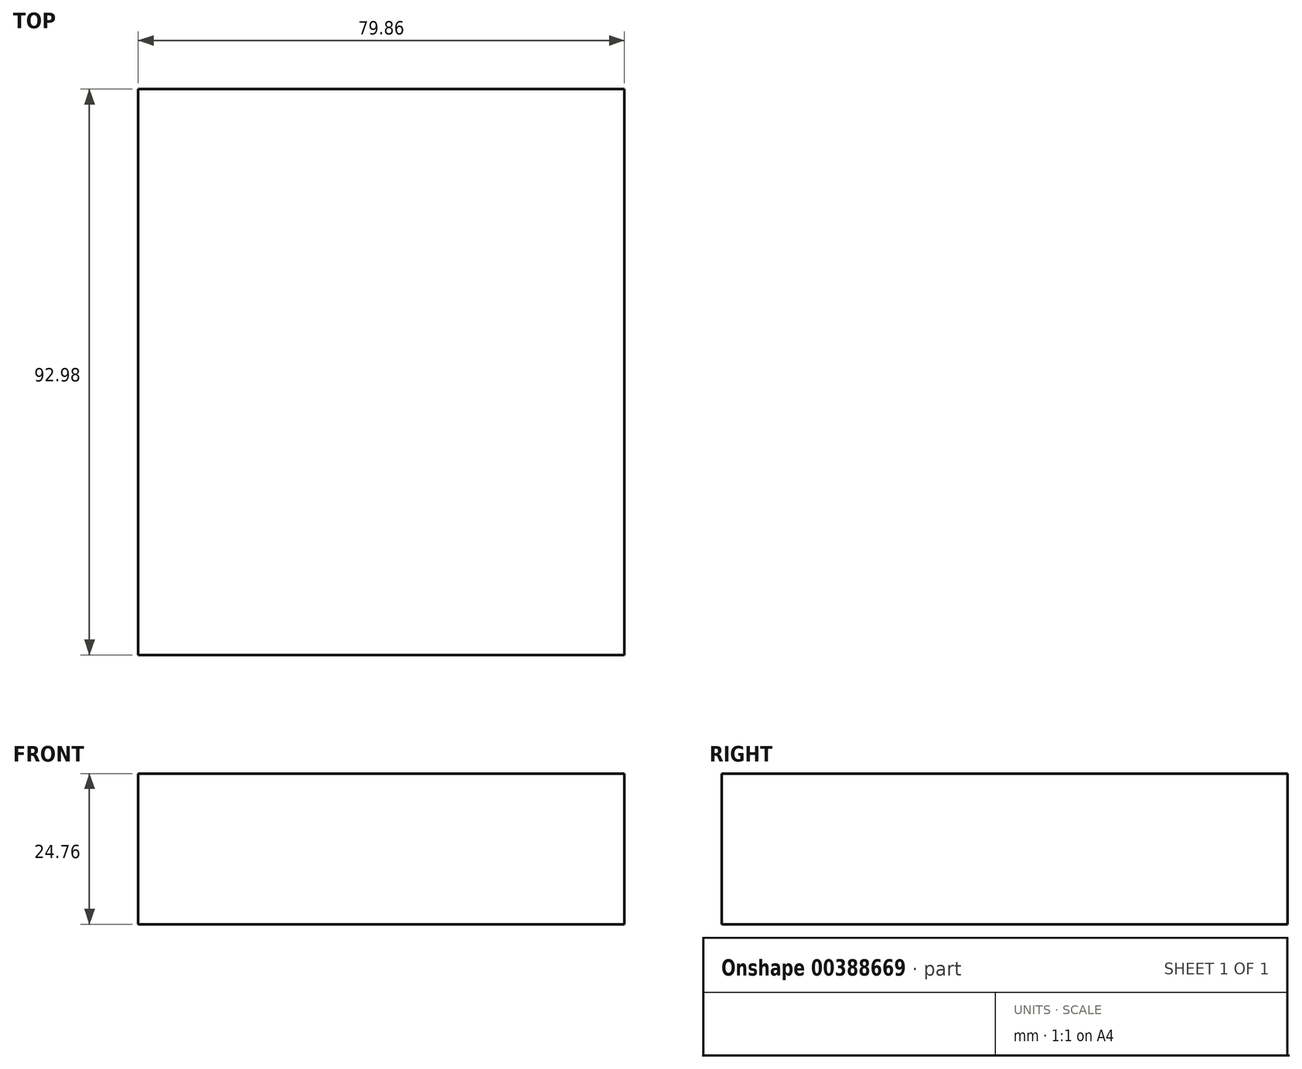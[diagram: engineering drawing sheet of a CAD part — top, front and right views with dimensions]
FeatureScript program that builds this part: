
annotation { "Feature Type Name" : "Feature", "Feature Type Description" : "" }
export const myFeature = defineFeature(function(context is Context, id is Id, definition is map)
    precondition{}
    {
        {
            var Q0;
            Q0=qCreatedBy(makeId("Front.planeOp"),FACE);
            var sketch = newSketch(context, id + "F0", { "sketchPlane" : qUnion([Q0])});
            skLineSegment(sketch, "E0.bottom", {"start": v(-62.5, -24.76) * mm, "end": v(17.35, -24.76) * mm});
            skLineSegment(sketch, "E0.top", {"start": v(-62.5, 0) * mm, "end": v(17.35, 0) * mm});
            skLineSegment(sketch, "E0.left", {"start": v(-62.5, -24.76) * mm, "end": v(-62.5, 0) * mm});
            skLineSegment(sketch, "E0.right", {"start": v(17.35, -24.76) * mm, "end": v(17.35, 0) * mm});
            skSolve(sketch);
        }
        {
            var Q0;
            Q0 = qSketchRegion(id + "F0", true);
            extrude(context, id + "F1", {"entities" : qUnion([Q0]), "oppositeDirection" : true, "depth" : 92.98 * mm});
        }
    });
